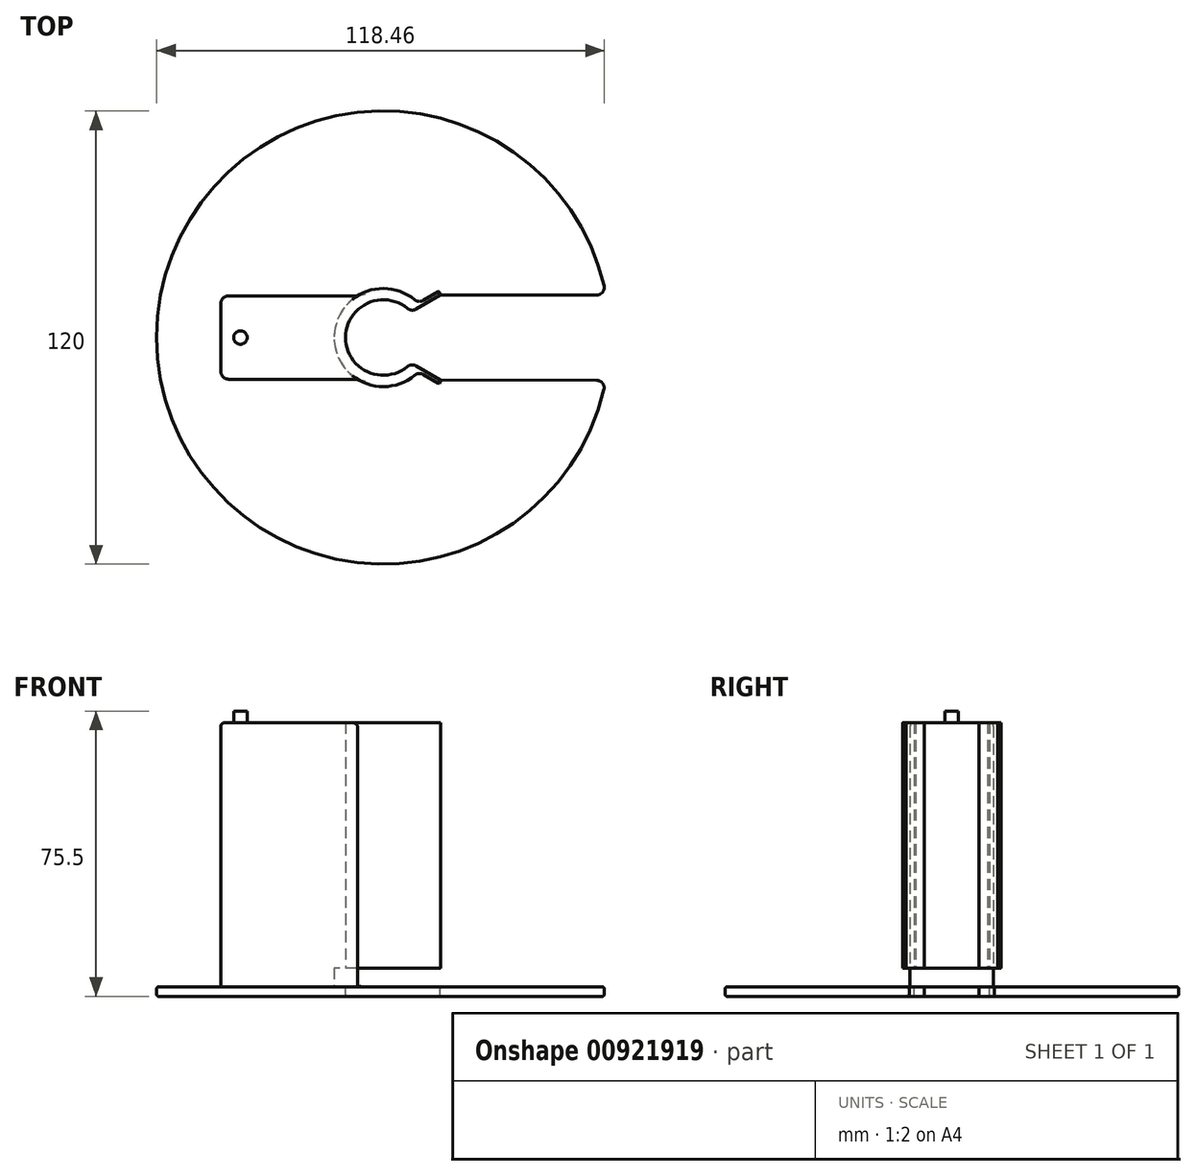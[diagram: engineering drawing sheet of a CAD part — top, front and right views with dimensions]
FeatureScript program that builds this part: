
annotation { "Feature Type Name" : "Feature", "Feature Type Description" : "" }
export const myFeature = defineFeature(function(context is Context, id is Id, definition is map)
    precondition{}
    {
        {
            var Q0;
            Q0=qCreatedBy(makeId("Top.planeOp"),FACE);
            var sketch = newSketch(context, id + "F0", { "sketchPlane" : qUnion([Q0])});
            skArc(sketch, "E0", {"start": v(6.39, 7.7) * mm, "mid": v(-10, 0) * mm, "end": v(6.39, -7.7) * mm});
            skArc(sketch, "E1.0", {"start": v(8.31, 10) * mm, "mid": v(-13, 0) * mm, "end": v(8.31, -10) * mm});
            skLineSegment(sketch, "E2", {"start": v(8.68, 7.51) * mm, "end": v(15.04, 11.26) * mm});
            skLineSegment(sketch, "E3.0", {"start": v(10.6, 9.8) * mm, "end": v(14.54, 12.12) * mm});
            skLineSegment(sketch, "E4", {"start": v(14.8, 12.05) * mm, "end": v(15.1, 11.51) * mm});
            skLineSegment(sketch, "E5.MirrorCS", {"start": v(8.68, -7.51) * mm, "end": v(15.04, -11.26) * mm});
            skLineSegment(sketch, "E6.MirrorCS", {"start": v(10.6, -9.8) * mm, "end": v(14.54, -12.12) * mm});
            skLineSegment(sketch, "E7.MirrorCS", {"start": v(14.8, -12.05) * mm, "end": v(15.1, -11.51) * mm});
            skPoint(sketch, "E8.visualSharp", {"position": v(7.38, 6.75) * mm});
            skArc(sketch, "E8.filletArc", {"start": v(6.39, 7.7) * mm, "mid": v(7.5, 7.24) * mm, "end": v(8.68, 7.51) * mm});
            skPoint(sketch, "E9.visualSharp", {"position": v(9.33, 9.05) * mm});
            skArc(sketch, "E9.filletArc", {"start": v(8.31, 10) * mm, "mid": v(9.43, 9.54) * mm, "end": v(10.6, 9.8) * mm});
            skPoint(sketch, "E10.visualSharp", {"position": v(7.38, -6.75) * mm});
            skArc(sketch, "E10.filletArc", {"start": v(8.68, -7.51) * mm, "mid": v(7.5, -7.24) * mm, "end": v(6.39, -7.7) * mm});
            skPoint(sketch, "E11.visualSharp", {"position": v(9.33, -9.05) * mm});
            skArc(sketch, "E11.filletArc", {"start": v(10.6, -9.8) * mm, "mid": v(9.43, -9.54) * mm, "end": v(8.31, -10) * mm});
            skPoint(sketch, "E12.visualSharp", {"position": v(15.2, 11.35) * mm});
            skArc(sketch, "E12.filletArc", {"start": v(15.04, 11.26) * mm, "mid": v(15.13, 11.37) * mm, "end": v(15.1, 11.51) * mm});
            skPoint(sketch, "E13.visualSharp", {"position": v(14.7, 12.21) * mm});
            skArc(sketch, "E13.filletArc", {"start": v(14.8, 12.05) * mm, "mid": v(14.68, 12.14) * mm, "end": v(14.54, 12.12) * mm});
            skPoint(sketch, "E14.visualSharp", {"position": v(15.2, -11.35) * mm});
            skArc(sketch, "E14.filletArc", {"start": v(15.1, -11.51) * mm, "mid": v(15.13, -11.37) * mm, "end": v(15.04, -11.26) * mm});
            skPoint(sketch, "E15.visualSharp", {"position": v(14.7, -12.21) * mm});
            skArc(sketch, "E15.filletArc", {"start": v(14.54, -12.12) * mm, "mid": v(14.68, -12.14) * mm, "end": v(14.8, -12.05) * mm});
            skPoint(sketch, "E16.endSnap0", {"position": v(-13, 0) * mm});
            skLineSegment(sketch, "E17", {"start": v(-43, 9.04) * mm, "end": v(-43, 0) * mm});
            skLineSegment(sketch, "E18", {"start": v(-6.87, 11.04) * mm, "end": v(-41, 11.04) * mm});
            skPoint(sketch, "E19.orphan", {"position": v(-43, 4.25) * mm});
            skLineSegment(sketch, "E20.MirrorCS", {"start": v(-6.87, -11.04) * mm, "end": v(-41, -11.04) * mm});
            skLineSegment(sketch, "E21.MirrorCS", {"start": v(-43, -9.04) * mm, "end": v(-43, 0) * mm});
            skPoint(sketch, "E22.visualSharp", {"position": v(-43, 11.04) * mm});
            skArc(sketch, "E22.filletArc", {"start": v(-41, 11.04) * mm, "mid": v(-42.41, 10.45) * mm, "end": v(-43, 9.04) * mm});
            skPoint(sketch, "E23.visualSharp", {"position": v(-43, -11.04) * mm});
            skArc(sketch, "E23.filletArc", {"start": v(-43, -9.04) * mm, "mid": v(-42.41, -10.45) * mm, "end": v(-41, -11.04) * mm});
            skArc(sketch, "E24", {"start": v(58.41, 13.71) * mm, "mid": v(-60, 0.05) * mm, "end": v(58.4, -13.8) * mm});
            skLineSegment(sketch, "E25", {"start": v(15.04, 11.26) * mm, "end": v(56.46, 11.26) * mm});
            skLineSegment(sketch, "E26", {"start": v(15.04, -11.26) * mm, "end": v(56.45, -11.35) * mm});
            skPoint(sketch, "E27.visualSharp", {"position": v(58.93, 11.26) * mm});
            skArc(sketch, "E27.filletArc", {"start": v(56.46, 11.26) * mm, "mid": v(58.03, 12.01) * mm, "end": v(58.41, 13.71) * mm});
            skPoint(sketch, "E28.visualSharp", {"position": v(58.92, -11.35) * mm});
            skArc(sketch, "E28.filletArc", {"start": v(58.4, -13.8) * mm, "mid": v(58.01, -12.1) * mm, "end": v(56.45, -11.35) * mm});
            skSolve(sketch);
        }
        {
            var Q0;
            Q0=makeQuery(id+"F0.imprint","IMPRINT",FACE,{"disambiguationData":[TD([[makeQuery(id+"F0.imprint","IMPRINT",EDGE,{"derivedFrom":sQuery(id+"F0.wireOp",EDGE,"E17")}),1.0]])]});
            extrude(context, id + "F1", {"entities" : qUnion([Q0]), "depth" : 70 * mm, "offsetDistance" : 25 * mm, "hasSecondDirection" : true, "secondDirectionOppositeDirection" : true, "secondDirectionDepth" : 2.5 * mm});
        }
        {
            var Q0;
            Q0=makeQuery(id+"F0.imprint","IMPRINT",FACE,{"disambiguationData":[TD([[makeQuery(id+"F0.imprint","IMPRINT",EDGE,{"derivedFrom":sQuery(id+"F0.wireOp",EDGE,"E0")}),-1.0]])]});
            extrude(context, id + "F2", {"entities" : qUnion([Q0]), "operationType" : NewBodyOperationType.ADD, "depth" : 70 * mm, "offsetDistance" : 25 * mm, "hasSecondDirection" : true, "secondDirectionOppositeDirection" : true, "secondDirectionDepth" : -5 * mm});
        }
        {
            var Q0;
            Q0=makeQuery(id+"F0.imprint","IMPRINT",FACE,{"disambiguationData":[TD([[makeQuery(id+"F0.imprint","IMPRINT",EDGE,{"derivedFrom":sQuery(id+"F0.wireOp",EDGE,"E3.0")}),1.0]])]});
            var Q1;
            Q1=makeQuery(id+"F0.imprint","IMPRINT",FACE,{"disambiguationData":[TD([[makeQuery(id+"F0.imprint","IMPRINT",EDGE,{"derivedFrom":sQuery(id+"F0.wireOp",EDGE,"E0")}),-1.0]])]});
            extrude(context, id + "F3", {"entities" : qUnion([Q0, Q1]), "oppositeDirection" : true, "depth" : 2.5 * mm, "offsetDistance" : 25 * mm});
        }
        {
            var Q0;
            Q0=makeQuery(id+"F1.opExtrude","CAP_EDGE",EDGE,{"disambiguationData":[OSD([sQuery(id+"F0.wireOp",EDGE,"E20.MirrorCS")])],"isStart":false});
            fillet(context, id + "F4", {"entities" : qUnion([Q0]), "radius" : 1 * mm, "tangentPropagation" : true, "allowEdgeOverflow" : false});
        }
        {
            var Q0;
            {var subQ0=sQuery(id+"F0.wireOp",EDGE,"E1.0");Q0=makeQuery(id+"F2.boolean.opBoolean","MERGE",FACE,{"derivedFrom":[makeQuery(id+"F1.opExtrude","CAP_FACE",FACE,{"disambiguationData":[OSD([subQ0,sQuery(id+"F0.wireOp",EDGE,"E17"),sQuery(id+"F0.wireOp",EDGE,"E18"),sQuery(id+"F0.wireOp",EDGE,"E20.MirrorCS"),sQuery(id+"F0.wireOp",EDGE,"E21.MirrorCS"),sQuery(id+"F0.wireOp",EDGE,"E22.filletArc"),sQuery(id+"F0.wireOp",EDGE,"E23.filletArc")])],"isStart":false}),makeQuery(id+"F2.opExtrude","CAP_FACE",FACE,{"disambiguationData":[OSD([sQuery(id+"F0.wireOp",EDGE,"E0"),subQ0,sQuery(id+"F0.wireOp",EDGE,"E2"),sQuery(id+"F0.wireOp",EDGE,"E3.0"),sQuery(id+"F0.wireOp",EDGE,"E4"),sQuery(id+"F0.wireOp",EDGE,"E5.MirrorCS"),sQuery(id+"F0.wireOp",EDGE,"E6.MirrorCS"),sQuery(id+"F0.wireOp",EDGE,"E7.MirrorCS"),sQuery(id+"F0.wireOp",EDGE,"E8.filletArc"),sQuery(id+"F0.wireOp",EDGE,"E9.filletArc"),sQuery(id+"F0.wireOp",EDGE,"E10.filletArc"),sQuery(id+"F0.wireOp",EDGE,"E11.filletArc"),sQuery(id+"F0.wireOp",EDGE,"E12.filletArc"),sQuery(id+"F0.wireOp",EDGE,"E13.filletArc"),sQuery(id+"F0.wireOp",EDGE,"E14.filletArc"),sQuery(id+"F0.wireOp",EDGE,"E15.filletArc")])],"isStart":false})]});}
            var sketch = newSketch(context, id + "F5", { "sketchPlane" : qUnion([Q0])});
            skCircle(sketch, "E29", {"center": v(-37.82, 0) * mm, "radius": 1.78 * mm});
            skPoint(sketch, "E29.centerSnap0", {"position": v(-42, 0) * mm});
            skSolve(sketch);
        }
        {
            var Q0;
            Q0 = qSketchRegion(id + "F5", true);
            extrude(context, id + "F6", {"entities" : qUnion([Q0]), "operationType" : NewBodyOperationType.ADD, "depth" : 3 * mm, "offsetDistance" : 25 * mm});
        }
        {
            var Q0;
            Q0=makeQuery(id+"F1.opExtrude","SWEPT_BODY",BODY,{"disambiguationData":[OSD([sQuery(id+"F0.wireOp",EDGE,"E1.0"),sQuery(id+"F0.wireOp",EDGE,"E17"),sQuery(id+"F0.wireOp",EDGE,"E18"),sQuery(id+"F0.wireOp",EDGE,"E20.MirrorCS"),sQuery(id+"F0.wireOp",EDGE,"E21.MirrorCS"),sQuery(id+"F0.wireOp",EDGE,"E22.filletArc"),sQuery(id+"F0.wireOp",EDGE,"E23.filletArc")])]});
            var Q1;
            Q1=makeQuery(id+"F3.opExtrude","SWEPT_BODY",BODY,{"disambiguationData":[OSD([sQuery(id+"F0.wireOp",EDGE,"E0"),sQuery(id+"F0.wireOp",EDGE,"E1.0"),sQuery(id+"F0.wireOp",EDGE,"E2"),sQuery(id+"F0.wireOp",EDGE,"E5.MirrorCS"),sQuery(id+"F0.wireOp",EDGE,"E8.filletArc"),sQuery(id+"F0.wireOp",EDGE,"E10.filletArc"),sQuery(id+"F0.wireOp",EDGE,"E17"),sQuery(id+"F0.wireOp",EDGE,"E18"),sQuery(id+"F0.wireOp",EDGE,"E20.MirrorCS"),sQuery(id+"F0.wireOp",EDGE,"E21.MirrorCS"),sQuery(id+"F0.wireOp",EDGE,"E22.filletArc"),sQuery(id+"F0.wireOp",EDGE,"E23.filletArc"),sQuery(id+"F0.wireOp",EDGE,"E24"),sQuery(id+"F0.wireOp",EDGE,"E25"),sQuery(id+"F0.wireOp",EDGE,"E26"),sQuery(id+"F0.wireOp",EDGE,"E27.filletArc"),sQuery(id+"F0.wireOp",EDGE,"E28.filletArc")])]});
            booleanBodies(context, id + "F7", {"operationType" : BooleanOperationType.UNION, "tools" : qUnion([Q0, Q1])});
        }
        {
            var Q0;
            Q0=makeQuery(id+"F3.opExtrude","CAP_FACE",FACE,{"disambiguationData":[OSD([sQuery(id+"F0.wireOp",EDGE,"E0"),sQuery(id+"F0.wireOp",EDGE,"E1.0"),sQuery(id+"F0.wireOp",EDGE,"E2"),sQuery(id+"F0.wireOp",EDGE,"E5.MirrorCS"),sQuery(id+"F0.wireOp",EDGE,"E8.filletArc"),sQuery(id+"F0.wireOp",EDGE,"E10.filletArc"),sQuery(id+"F0.wireOp",EDGE,"E17"),sQuery(id+"F0.wireOp",EDGE,"E18"),sQuery(id+"F0.wireOp",EDGE,"E20.MirrorCS"),sQuery(id+"F0.wireOp",EDGE,"E21.MirrorCS"),sQuery(id+"F0.wireOp",EDGE,"E22.filletArc"),sQuery(id+"F0.wireOp",EDGE,"E23.filletArc"),sQuery(id+"F0.wireOp",EDGE,"E24"),sQuery(id+"F0.wireOp",EDGE,"E25"),sQuery(id+"F0.wireOp",EDGE,"E26"),sQuery(id+"F0.wireOp",EDGE,"E27.filletArc"),sQuery(id+"F0.wireOp",EDGE,"E28.filletArc")])],"isStart":true});
            var Q1;
            {var subQ0=sQuery(id+"F0.wireOp",EDGE,"E23.filletArc");var subQ1=sQuery(id+"F0.wireOp",EDGE,"E22.filletArc");var subQ2=sQuery(id+"F0.wireOp",EDGE,"E21.MirrorCS");var subQ3=sQuery(id+"F0.wireOp",EDGE,"E20.MirrorCS");var subQ4=sQuery(id+"F0.wireOp",EDGE,"E18");var subQ5=sQuery(id+"F0.wireOp",EDGE,"E17");var subQ6=sQuery(id+"F0.wireOp",EDGE,"E1.0");Q1=makeQuery(id+"F7.opBoolean","MERGE",FACE,{"derivedFrom":[makeQuery(id+"F1.opExtrude","CAP_FACE",FACE,{"disambiguationData":[OSD([subQ6,subQ5,subQ4,subQ3,subQ2,subQ1,subQ0])],"isStart":true}),makeQuery(id+"F3.opExtrude","CAP_FACE",FACE,{"disambiguationData":[OSD([sQuery(id+"F0.wireOp",EDGE,"E0"),subQ6,sQuery(id+"F0.wireOp",EDGE,"E2"),sQuery(id+"F0.wireOp",EDGE,"E5.MirrorCS"),sQuery(id+"F0.wireOp",EDGE,"E8.filletArc"),sQuery(id+"F0.wireOp",EDGE,"E10.filletArc"),subQ5,subQ4,subQ3,subQ2,subQ1,subQ0,sQuery(id+"F0.wireOp",EDGE,"E24"),sQuery(id+"F0.wireOp",EDGE,"E25"),sQuery(id+"F0.wireOp",EDGE,"E26"),sQuery(id+"F0.wireOp",EDGE,"E27.filletArc"),sQuery(id+"F0.wireOp",EDGE,"E28.filletArc")])],"isStart":false})]});}
            fillet(context, id + "F8", {"entities" : qUnion([Q0, Q1]), "radius" : .5 * mm, "tangentPropagation" : true, "allowEdgeOverflow" : false});
        }
    });
